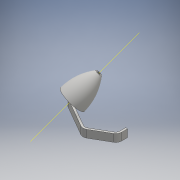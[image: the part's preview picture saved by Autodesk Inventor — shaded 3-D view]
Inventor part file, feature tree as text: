
AUTODESK INVENTOR PART (.ipt)
format: ipt  version: 2016 SP1 (Build 200210100, 210)  size: 359,424 bytes
history: native  units: mm
features: sketch x16, extrude x15, projected_geometry x5, reference x4, plane x3, mirror x2, revolve x1, fillet x1, other x1
ambient origin geometry x8: Origin, YZ Plane, XZ Plane, XY Plane, X Axis, Y Axis, Z Axis, Center Point
bodies: Solid1 (feature_tree)
feature tree (48):
  extrude  "Extrusion1"  Depth=0.5mm
  plane  "Work Plane1"
  sketch  "Sketch3"  dims[d4=0.5mm d7=0.5mm]
  plane  "Work Plane2"
  plane  "Work Plane3"
  revolve  "Revolution2"  [1 undecoded]
  extrude  "Extrusion4"  Depth=10.0mm
  extrude  "Extrusion5"  Depth=10.0mm TaperAngle=0.0deg
  extrude  "Extrusion6"  Depth=10.0mm TaperAngle=0.0deg
  extrude  "Extrusion7"  Depth=10.0mm TaperAngle=0.0deg
  extrude  "Extrusion8"  Depth=45.0mm TaperAngle=0.0deg
  extrude  "Extrusion10"  Depth=0.1mm TaperAngle=0.0deg
  extrude  "Extrusion11"  Depth=16.0mm TaperAngle=0.0deg
  extrude  "Extrusion12"  Depth=10.0mm
  extrude  "Extrusion14"  Depth=3.0mm
  extrude  "Extrusion15"  Depth=5.0mm TaperAngle=0.0deg
  mirror  "Mirror2"
  extrude  "Extrusion16"  Depth=5.0mm TaperAngle=0.0deg
  extrude  "Extrusion17"  [1 undecoded]
  fillet  "Fillet1"  [1 undecoded]
  extrude  "Extrusion18"  [1 undecoded]
  mirror  "Mirror3"
  extrude  "Extrusion19"  [1 undecoded]
  sketch  "Sketch1"  dims[d0=2.0mm d3=0.5mm]
  reference  "Reference1"
  reference  "Reference2"
  reference  "Reference3"
  reference  "Reference4"
  other  "Work Axis1"
  sketch  "Sketch5"  dims[d8=10.0mm d9=0.0mm d13=1.5mm]
  sketch  "Sketch7"  dims[d14=90.0deg d19=10.0mm d20=0.0mm]
  sketch  "Sketch8"  dims[d21=10.0mm d22=0.0mm d23=10.0mm d24=0.0mm]
  projected_geometry  "Projected Loop3"
  sketch  "Sketch9"  dims[d25=10.0mm d26=0.0mm d27=10.0mm d28=0.0mm]
  sketch  "Sketch10"  dims[d31=45.0mm d32=0.0mm d33=45.0mm d34=0.0mm]
  projected_geometry  "Projected Loop4"
  projected_geometry  "Projected Loop5"
  sketch  "Sketch11"  dims[d35=45.0mm d36=0.0mm d39=0.1mm d40=0.0mm]
  sketch  "Sketch12"  dims[d41=25.0mm d42=16.0mm d43=0.0mm]
  sketch  "Sketch14"  dims[d44=10.0mm d45=0.0mm d46=9.0mm]
  projected_geometry  "Projected Loop9"
  sketch  "Sketch16"  dims[d47=6.0mm d48=3.0mm]
  projected_geometry  "Projected Loop11"
  sketch  "Sketch17"  dims[d49=30.0mm d51=360.0deg d53=5.0mm d54=0.0mm]
  sketch  "Sketch18"  dims[d55=2.0mm d56=5.0mm d57=0.0mm]
  sketch  "Sketch19"  dims[d58=5.0mm d59=0.0mm]
  sketch  "Sketch21"
  sketch  "Sketch23"
note: 5 required parameter values undecoded (feature->parameter linkage not recoverable at this tier; creation-order binding heuristic only, values carry confidence <= 0.55)